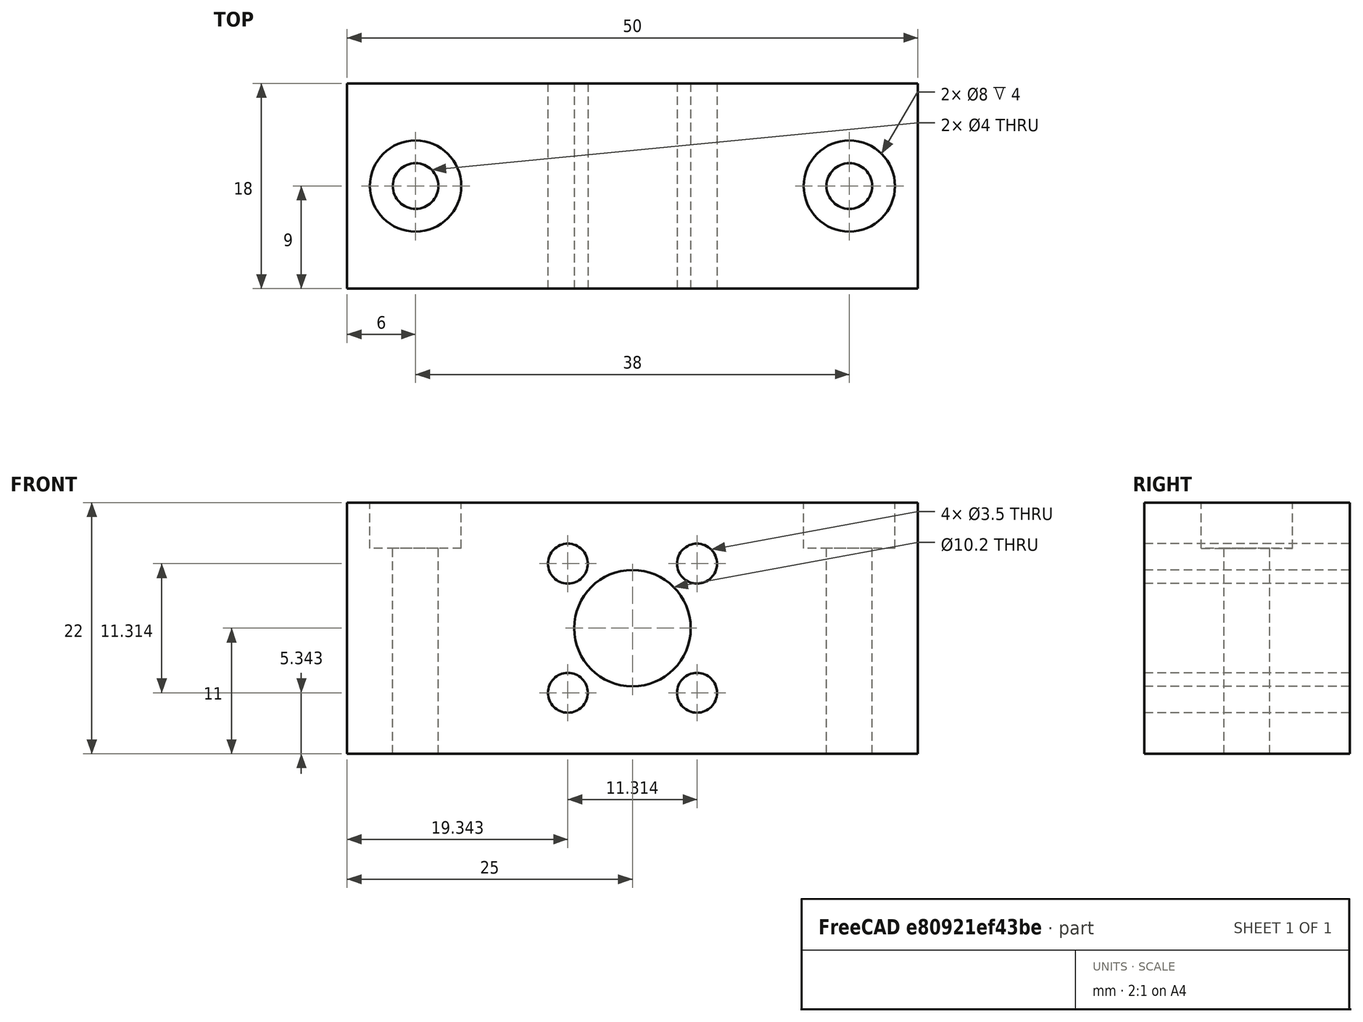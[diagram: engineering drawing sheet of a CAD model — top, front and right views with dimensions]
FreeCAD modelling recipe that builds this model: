
FCSTD DOCUMENT  (FreeCAD 0.17R13541 (Git))
Label: T8LeadScrewNut
License: All rights reserved
LicenseURL: http://en.wikipedia.org/wiki/All_rights_reserved
objects: Part::Cylinder×4, Part::Cut×4, Part::FeaturePython×3, Part::Feature×2, Part::Box×1, Part::MultiFuse×1
note: 15 computed .brp shape members not serialized (recipe doc carries the construction recipe); baked Part::Feature solids carry a one-line shape summary decoded from their .brp

FEATURE [Part::Cylinder] Cylinder  label="Cilindro"
  Angle = 360
  AttacherType = Attacher::AttachEngine3D
  Height = 25
  Radius = 1.75
FEATURE [Part::Box] Box  label="Cubo"
  AttacherType = Attacher::AttachEngine3D
  Height = 22
  Length = 50
  Width = 18
FEATURE [Part::Cylinder] Cylinder001  label="Cilindro001"
  Angle = 360
  AttacherType = Attacher::AttachEngine3D
  Height = 30
  Radius = 2
FEATURE [Part::FeaturePython] Array001  # Draft array (typed FeaturePython)
  Angle = 360
  ArrayType = 0
  Axis = (0,0,1)
  Base = -> Cylinder001
  Center = (0,0,0)
  Fuse = false
  IntervalAxis = (0,0,0)
  IntervalX = (38,0,0)
  IntervalY = (0,1,0)
  IntervalZ = (0,0,0)
  NumberPolar = 1
  NumberX = 2
  NumberY = 1
  NumberZ = 1
  Placement = pos=(6,9,-8) rot=(0,0,1;0rad)
FEATURE [Part::Cylinder] Cylinder002  label="Cilindro002"
  Angle = 360
  AttacherType = Attacher::AttachEngine3D
  Height = 30
  Placement = pos=(25,30,11) rot=(1,0,0;1.5708rad)
  Radius = 5.1
FEATURE [Part::FeaturePython] Array002  # Draft array (typed FeaturePython)
  Angle = 360
  ArrayType = 0
  Axis = (0,0,1)
  Base = -> Cylinder
  Center = (0,0,0)
  Fuse = false
  IntervalAxis = (0,0,0)
  IntervalX = (16,0,0)
  IntervalY = (0,1,0)
  IntervalZ = (0,0,0)
  NumberPolar = 1
  NumberX = 2
  NumberY = 1
  NumberZ = 1
  Placement = pos=(-33.5045,5.9016,-8.71211) rot=(0,0,1;0rad)
FEATURE [Part::Feature] Array002001  label="Array003"
  Placement = pos=(-25.5045,-2.0984,-8.71211) rot=(0,0,1;1.5708rad)
  shape: bbox 3.5 x 19.5 x 25 mm, 6 faces, 2 solids (baked)
FEATURE [Part::MultiFuse] Fusion
  Placement = pos=(38.8613,16.2879,-11.2074) rot=(0.862856,0.357407,-0.357407;1.71777rad)
  Refine = true
  Shapes = -> [Array002001,Array002]
FEATURE [Part::Cut] Cut
  Base = -> Box
  Refine = true
  Tool = -> Cylinder002
FEATURE [Part::Cut] Cut001
  Base = -> Cut
  Refine = true
  Tool = -> Fusion
FEATURE [Part::Cut] Cut002  label="T8LeadScrewNut-Terminado"
  Base = -> Cut001
  Refine = true
  Tool = -> Array001
FEATURE [Part::Cylinder] Cylinder003  label="Cilindro003"
  Angle = 360
  AttacherType = Attacher::AttachEngine3D
  Height = 4
  Radius = 4
FEATURE [Part::FeaturePython] Array  # Draft array (typed FeaturePython)
  Angle = 360
  ArrayType = 0
  Axis = (0,0,1)
  Base = -> Cylinder003
  Center = (0,0,0)
  Fuse = false
  IntervalAxis = (0,0,0)
  IntervalX = (38,0,0)
  IntervalY = (0,1,0)
  IntervalZ = (0,0,0)
  NumberPolar = 1
  NumberX = 2
  NumberY = 1
  NumberZ = 1
  Placement = pos=(6,9,18) rot=(0,0,1;0rad)
FEATURE [Part::Cut] Cut002002  label="T8LeadScrewNut-Terminado001"
  Base = -> Cut002
  Refine = true
  Tool = -> Array
FEATURE [Part::Feature] Cut002002001  label="T8LeadScrewNut-Copia"
  shape: bbox 50 x 18 x 22 mm, 17 faces (baked)
